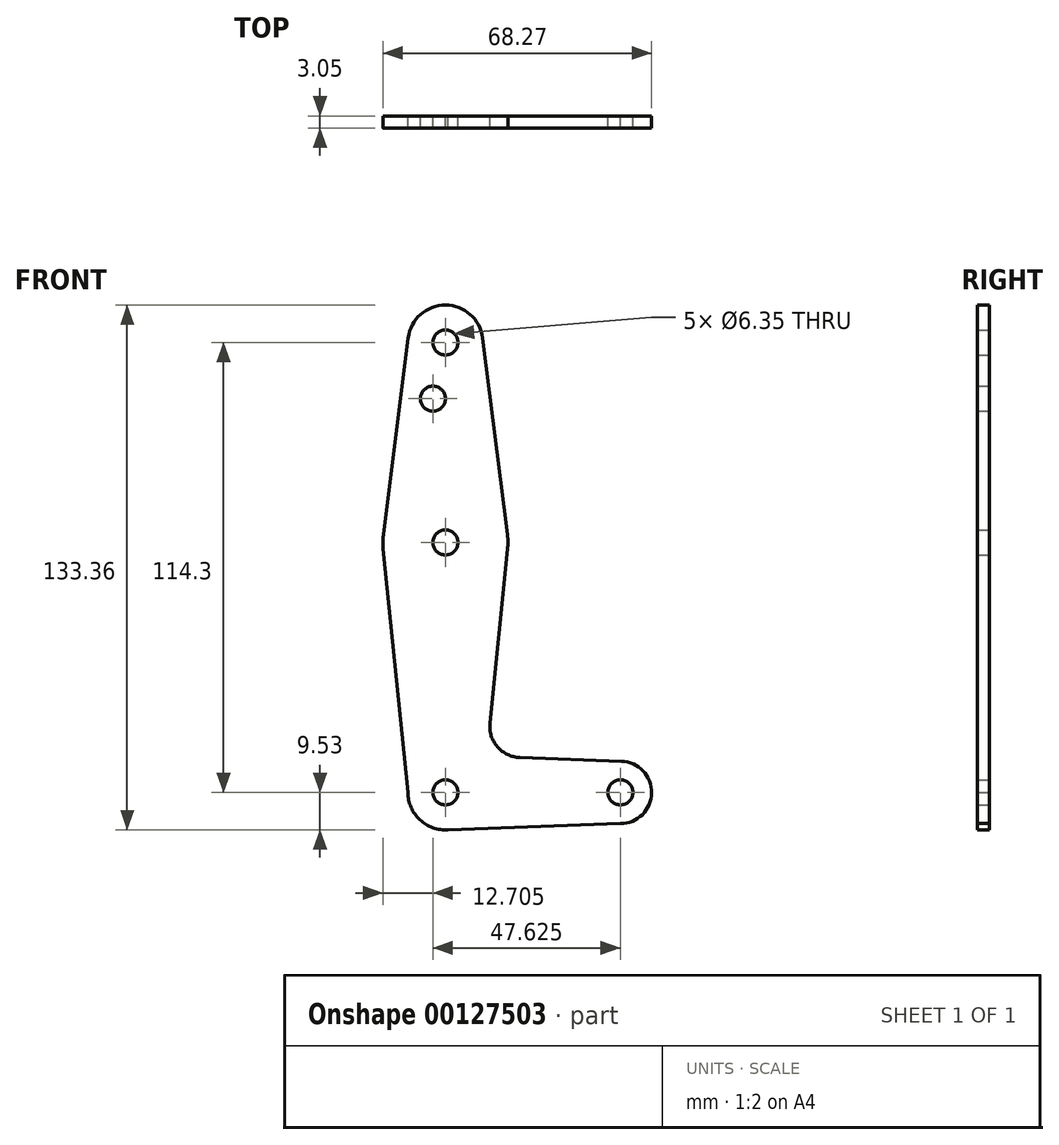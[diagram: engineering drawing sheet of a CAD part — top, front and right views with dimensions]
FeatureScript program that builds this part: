
annotation { "Feature Type Name" : "Feature", "Feature Type Description" : "" }
export const myFeature = defineFeature(function(context is Context, id is Id, definition is map)
    precondition{}
    {
        {
            var Q0;
            Q0=qCreatedBy(makeId("Front.planeOp"),FACE);
            var sketch = newSketch(context, id + "F0", { "sketchPlane" : qUnion([Q0])});
            skLineSegment(sketch, "E0", {"start": v(0, 0) * mm, "end": v(0, 114.3) * mm, "construction": true});
            skLineSegment(sketch, "E1", {"start": v(0, 0) * mm, "end": v(44.45, 0) * mm, "construction": true});
            skCircle(sketch, "E2", {"center": v(0, 114.3) * mm, "radius": 9.53 * mm});
            skCircle(sketch, "E3", {"center": v(0, 63.5) * mm, "radius": 15.88 * mm});
            skCircle(sketch, "E4", {"center": v(0, 0) * mm, "radius": 9.53 * mm});
            skCircle(sketch, "E5", {"center": v(44.45, 0) * mm, "radius": 7.94 * mm});
            skLineSegment(sketch, "E6", {"start": v(-9.45, 115.5) * mm, "end": v(-15.75, 65.48) * mm});
            skLineSegment(sketch, "E7", {"start": v(9.45, 115.5) * mm, "end": v(15.75, 65.48) * mm});
            skLineSegment(sketch, "E8", {"start": v(-9.53, 0) * mm, "end": v(-15.8, 61.9) * mm});
            skLineSegment(sketch, "E9", {"start": v(11.3, 17.6) * mm, "end": v(15.8, 61.9) * mm});
            skLineSegment(sketch, "E10", {"start": v(18.93, 8.85) * mm, "end": v(44.73, 7.93) * mm});
            skLineSegment(sketch, "E11", {"start": v(0, -9.53) * mm, "end": v(44.45, -7.94) * mm});
            skCircle(sketch, "E12", {"center": v(0, 114.3) * mm, "radius": 3.18 * mm});
            skCircle(sketch, "E13", {"center": v(0, 63.5) * mm, "radius": 3.18 * mm});
            skCircle(sketch, "E14", {"center": v(0, 0) * mm, "radius": 3.18 * mm});
            skCircle(sketch, "E15", {"center": v(44.45, 0) * mm, "radius": 3.18 * mm});
            skCircle(sketch, "E16", {"center": v(-3.18, 100.03) * mm, "radius": 3.18 * mm});
            skArc(sketch, "E17.filletArc", {"start": v(11.3, 17.6) * mm, "mid": v(13.22, 11.57) * mm, "end": v(18.93, 8.85) * mm});
            skSolve(sketch);
        }
        {
            var Q0;
            Q0 = qSketchRegion(id + "F0", true);
            extrude(context, id + "F1", {"entities" : qUnion([Q0]), "depth" : 3.05 * mm});
        }
    });
